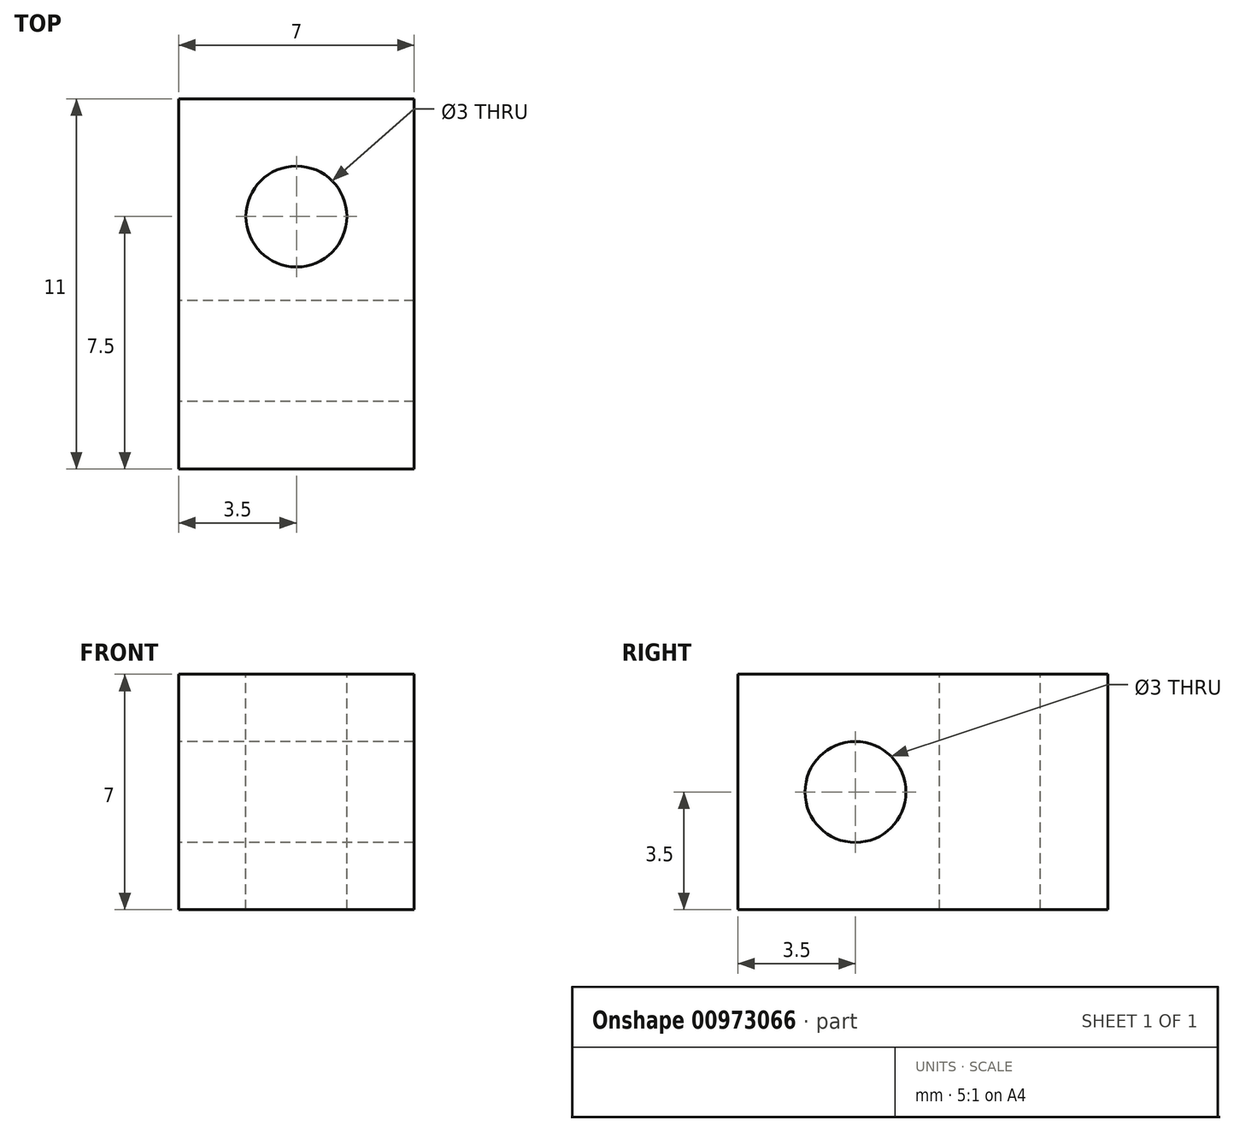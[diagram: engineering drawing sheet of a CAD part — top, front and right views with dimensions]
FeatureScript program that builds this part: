
annotation { "Feature Type Name" : "Feature", "Feature Type Description" : "" }
export const myFeature = defineFeature(function(context is Context, id is Id, definition is map)
    precondition{}
    {
        {
            var Q0;
            Q0=qCreatedBy(makeId("Top.planeOp"),FACE);
            var sketch = newSketch(context, id + "F0", { "sketchPlane" : qUnion([Q0])});
            skLineSegment(sketch, "E0.bottom", {"start": v(3.5, -5.5) * mm, "end": v(-3.5, -5.5) * mm});
            skLineSegment(sketch, "E0.top", {"start": v(3.5, 5.5) * mm, "end": v(-3.5, 5.5) * mm});
            skLineSegment(sketch, "E0.left", {"start": v(3.5, -5.5) * mm, "end": v(3.5, 5.5) * mm});
            skLineSegment(sketch, "E0.right", {"start": v(-3.5, -5.5) * mm, "end": v(-3.5, 5.5) * mm});
            skPoint(sketch, "E0.middle", {"position": v(0, 0) * mm});
            skSolve(sketch);
        }
        {
            var Q0;
            Q0 = qSketchRegion(id + "F0", true);
            extrude(context, id + "F1", {"entities" : qUnion([Q0]), "depth" : 7 * mm, "offsetDistance" : 25 * mm});
        }
        {
            var Q0;
            Q0=makeQuery(id+"F1.opExtrude","CAP_FACE",FACE,{"disambiguationData":[OSD([sQuery(id+"F0.wireOp",EDGE,"E0.bottom"),sQuery(id+"F0.wireOp",EDGE,"E0.top"),sQuery(id+"F0.wireOp",EDGE,"E0.left"),sQuery(id+"F0.wireOp",EDGE,"E0.right")])],"isStart":false});
            var sketch = newSketch(context, id + "F2", { "sketchPlane" : qUnion([Q0])});
            skCircle(sketch, "E1", {"center": v(0, 2) * mm, "radius": 1.5 * mm});
            skLineSegment(sketch, "E2", {"start": v(-3.5, 2) * mm, "end": v(3.5, 2) * mm, "construction": true});
            skSolve(sketch);
        }
        {
            var Q0;
            Q0 = qSketchRegion(id + "F2", true);
            var Q1;
            Q1 = qConstructionFilter(qBodyType(qCreatedBy(id + "F2" ,EDGE), BodyType.WIRE), ConstructionObject.NO);
            extrude(context, id + "F3", {"entities" : qUnion([Q0]), "operationType" : NewBodyOperationType.REMOVE, "surfaceEntities" : qUnion([Q1]), "endBound" : BoundingType.THROUGH_ALL, "oppositeDirection" : true, "depth" : 25 * mm, "offsetDistance" : 25 * mm});
        }
        {
            var Q0;
            Q0=makeQuery(id+"F1.opExtrude","SWEPT_FACE",FACE,{"disambiguationData":[OSD([sQuery(id+"F0.wireOp",EDGE,"E0.right")])]});
            var sketch = newSketch(context, id + "F4", { "sketchPlane" : qUnion([Q0])});
            skCircle(sketch, "E3", {"center": v(2, 3.5) * mm, "radius": 1.5 * mm});
            skLineSegment(sketch, "E4", {"start": v(2, 7) * mm, "end": v(2, 0) * mm, "construction": true});
            skSolve(sketch);
        }
        {
            var Q0;
            Q0 = qSketchRegion(id + "F4", true);
            extrude(context, id + "F5", {"entities" : qUnion([Q0]), "operationType" : NewBodyOperationType.REMOVE, "oppositeDirection" : true, "depth" : 25 * mm, "offsetDistance" : 25 * mm});
        }
    });
